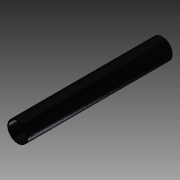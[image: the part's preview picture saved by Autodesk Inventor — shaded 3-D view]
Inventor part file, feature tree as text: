
AUTODESK INVENTOR PART (.ipt)
format: ipt  version: 2013 (Build 170138000, 138)  size: 79,360 bytes
history: native  units: in
note: dims shown in document units (in); Inventor stores cm internally (conversion verified against a paired STEP export)
features: extrude x2, sketch x2
ambient origin geometry x8: Origin, YZ Plane, XZ Plane, XY Plane, X Axis, Y Axis, Z Axis, Center Point
bodies: Solid1 (feature_tree)
feature tree (4):
  extrude  "Extrusion1"  Depth=8.0in TaperAngle=0.0deg
  extrude  "Extrusion3"  Depth=8.0in TaperAngle=0.0deg
  sketch  "Sketch1"  dims[d0=1.15in d1=8.0in d2=0.0in]
  sketch  "Sketch3"  dims[d10=1.0in d11=8.0in d12=0.0in]
